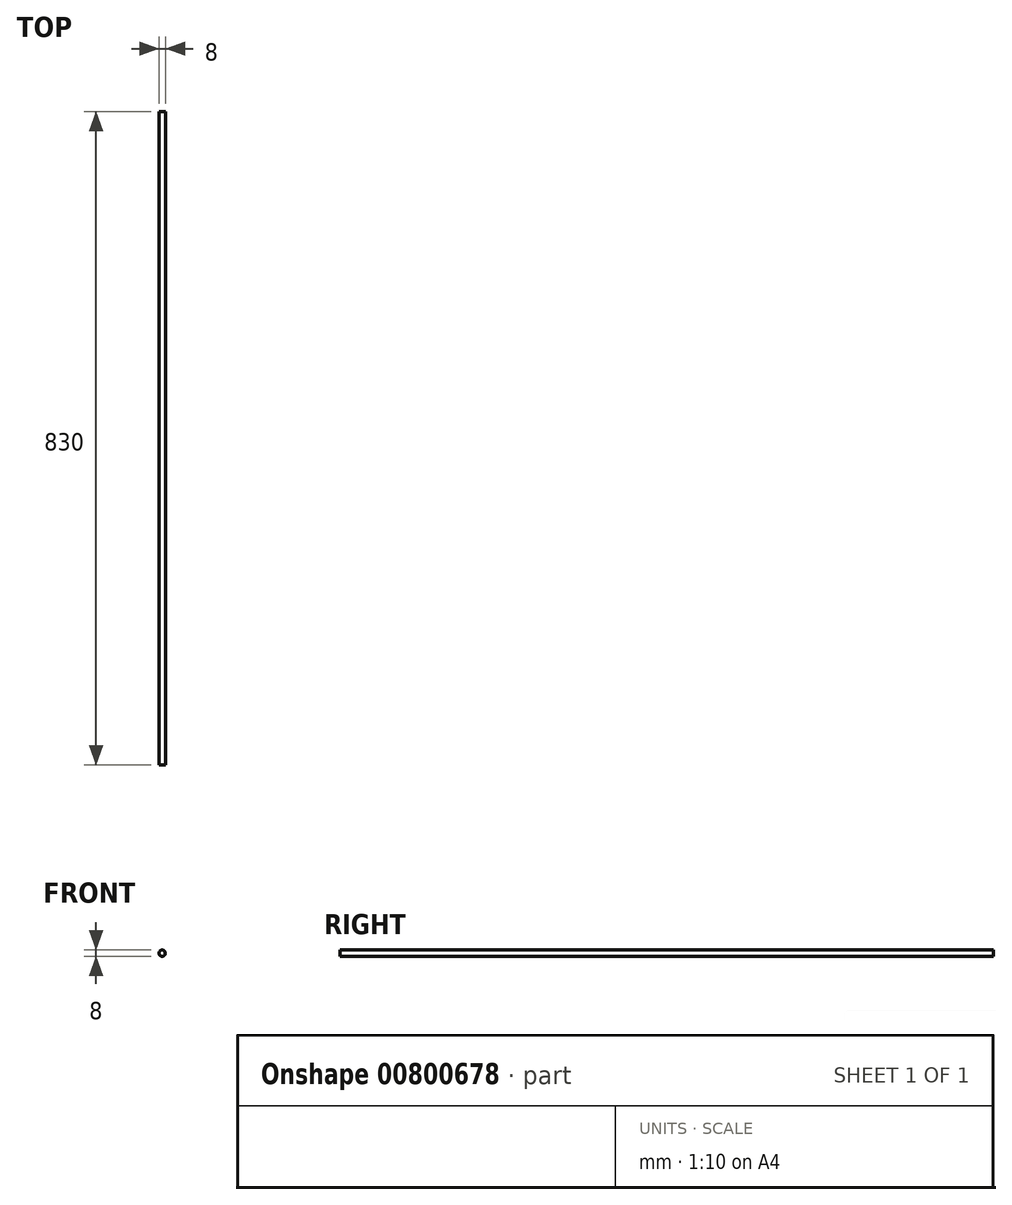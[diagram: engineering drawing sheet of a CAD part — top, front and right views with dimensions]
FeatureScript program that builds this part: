
annotation { "Feature Type Name" : "Feature", "Feature Type Description" : "" }
export const myFeature = defineFeature(function(context is Context, id is Id, definition is map)
    precondition{}
    {
        {
            var Q0;
            Q0=qCreatedBy(makeId("Front.planeOp"),FACE);
            var sketch = newSketch(context, id + "F0", { "sketchPlane" : qUnion([Q0])});
            skCircle(sketch, "E0", {"center": v(0, 0) * mm, "radius": 4 * mm});
            skSolve(sketch);
        }
        {
            var Q0;
            Q0=makeQuery(id+"F0.imprint","IMPRINT",FACE,{"disambiguationData":[TD([[makeQuery(id+"F0.imprint","IMPRINT",EDGE,{"derivedFrom":sQuery(id+"F0.wireOp",EDGE,"E0")}),1.0]])]});
            extrude(context, id + "F1", {"entities" : qUnion([Q0]), "endBound" : BoundingType.SYMMETRIC, "depth" : 830 * mm, "offsetDistance" : 25 * mm});
        }
    });
